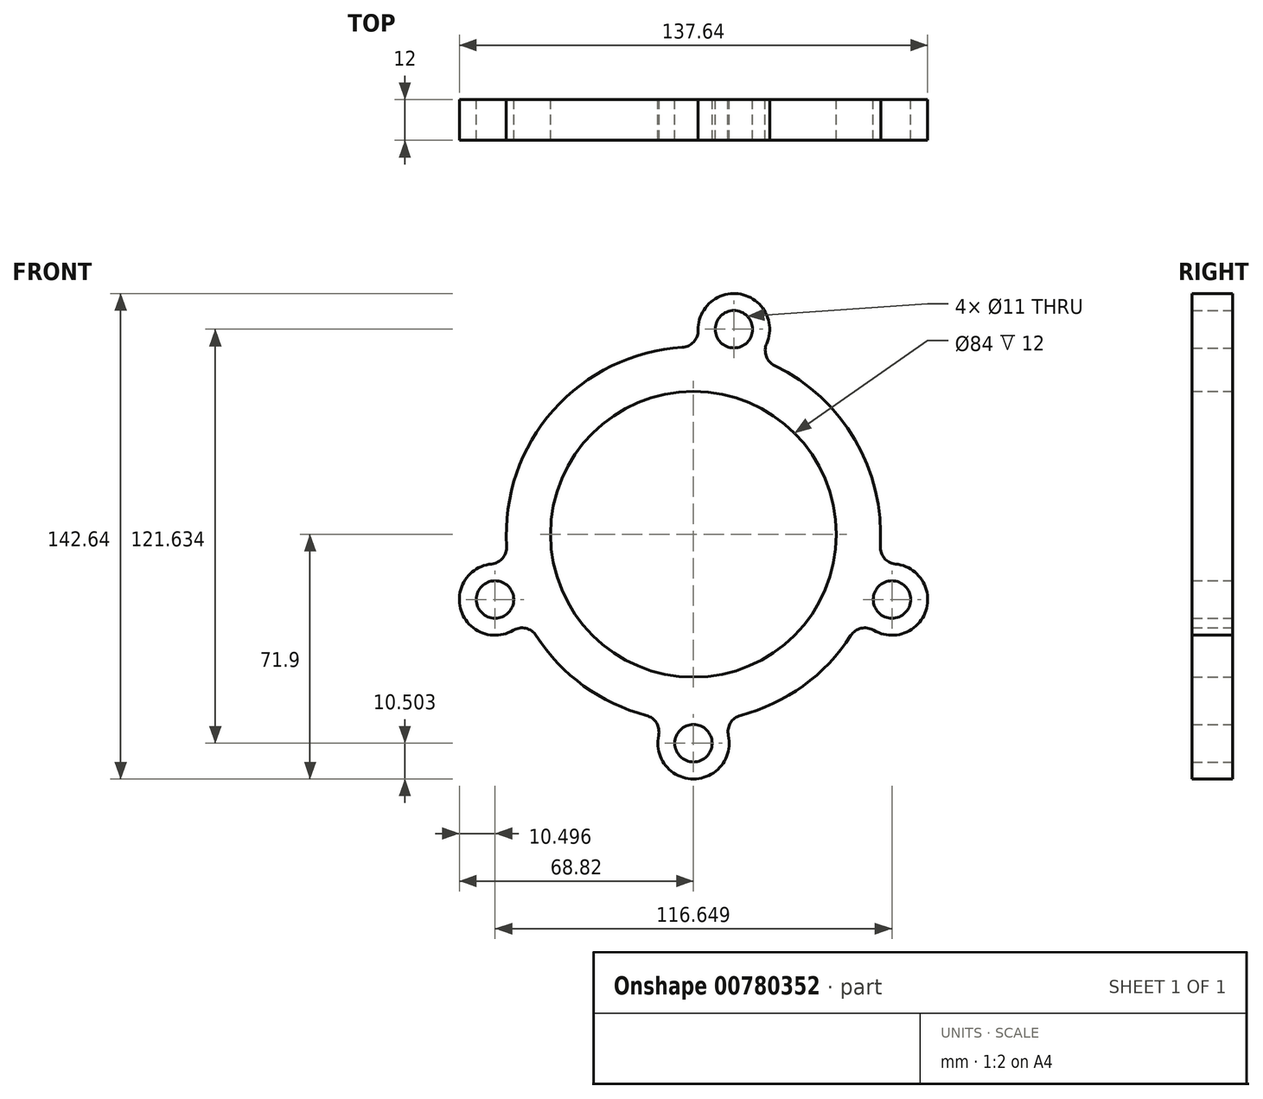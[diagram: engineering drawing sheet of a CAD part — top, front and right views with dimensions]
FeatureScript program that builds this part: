
annotation { "Feature Type Name" : "Feature", "Feature Type Description" : "" }
export const myFeature = defineFeature(function(context is Context, id is Id, definition is map)
    precondition{}
    {
        {
            var Q0;
            Q0=qCreatedBy(makeId("Front.planeOp"),FACE);
            var sketch = newSketch(context, id + "F0", { "sketchPlane" : qUnion([Q0])});
            skCircle(sketch, "E0", {"center": v(0, 0) * mm, "radius": 42 * mm});
            skArc(sketch, "E1.0", {"start": v(-46.22, -29.8) * mm, "mid": v(-32.25, -44.55) * mm, "end": v(-13.87, -53.22) * mm});
            skLineSegment(sketch, "E2", {"start": v(0, 0) * mm, "end": v(-58.32, -19.18) * mm, "construction": true});
            skCircle(sketch, "E3", {"center": v(-58.32, -19.18) * mm, "radius": 5.5 * mm});
            skArc(sketch, "E4.0", {"start": v(-59.38, -8.73) * mm, "mid": v(-68.3, -22.46) * mm, "end": v(-52.97, -28.21) * mm});
            skPoint(sketch, "E5.visualSharp", {"position": v(-49.26, -24.47) * mm});
            skArc(sketch, "E5.filletArc", {"start": v(-46.22, -29.8) * mm, "mid": v(-49.28, -27.65) * mm, "end": v(-52.97, -28.21) * mm});
            skPoint(sketch, "E6.visualSharp", {"position": v(-54.17, -9.54) * mm});
            skArc(sketch, "E6.filletArc", {"start": v(-59.38, -8.73) * mm, "mid": v(-56.07, -7) * mm, "end": v(-54.9, -3.45) * mm});
            skLineSegment(sketch, "E7", {"start": v(0, 0) * mm, "end": v(11.88, 60.24) * mm, "construction": true});
            skLineSegment(sketch, "E8", {"start": v(0, 0) * mm, "end": v(58.32, -19.18) * mm, "construction": true});
            skCircle(sketch, "E9", {"center": v(58.32, -19.18) * mm, "radius": 5.5 * mm});
            skCircle(sketch, "E10", {"center": v(11.88, 60.24) * mm, "radius": 5.5 * mm});
            skLineSegment(sketch, "E11", {"start": v(0, 0) * mm, "end": v(0, -61.4) * mm, "construction": true});
            skCircle(sketch, "E12", {"center": v(0, -61.4) * mm, "radius": 5.5 * mm});
            skArc(sketch, "E13.0", {"start": v(-10.25, -59.14) * mm, "mid": v(0, -71.9) * mm, "end": v(10.25, -59.14) * mm});
            skArc(sketch, "E14.0", {"start": v(52.97, -28.21) * mm, "mid": v(68.3, -22.46) * mm, "end": v(59.38, -8.73) * mm});
            skArc(sketch, "E15.0", {"start": v(21.5, 56.03) * mm, "mid": v(13.91, 70.54) * mm, "end": v(1.38, 60) * mm});
            skArc(sketch, "E16.trimOffspring", {"start": v(13.87, -53.22) * mm, "mid": v(32.25, -44.55) * mm, "end": v(46.22, -29.8) * mm});
            skArc(sketch, "E17.trimOffspring", {"start": v(54.9, -3.45) * mm, "mid": v(47.48, 27.76) * mm, "end": v(23.91, 49.53) * mm});
            skArc(sketch, "E18.trimOffspring", {"start": v(-3.31, 54.9) * mm, "mid": v(-41.2, 36.43) * mm, "end": v(-54.9, -3.45) * mm});
            skPoint(sketch, "E19.visualSharp", {"position": v(-7.86, -54.44) * mm});
            skArc(sketch, "E19.filletArc", {"start": v(-10.25, -59.14) * mm, "mid": v(-10.87, -55.45) * mm, "end": v(-13.87, -53.22) * mm});
            skPoint(sketch, "E20.visualSharp", {"position": v(7.86, -54.44) * mm});
            skArc(sketch, "E20.filletArc", {"start": v(13.87, -53.22) * mm, "mid": v(10.87, -55.45) * mm, "end": v(10.25, -59.14) * mm});
            skPoint(sketch, "E21.visualSharp", {"position": v(49.26, -24.47) * mm});
            skArc(sketch, "E21.filletArc", {"start": v(52.97, -28.21) * mm, "mid": v(49.28, -27.65) * mm, "end": v(46.22, -29.8) * mm});
            skPoint(sketch, "E22.visualSharp", {"position": v(54.17, -9.54) * mm});
            skArc(sketch, "E22.filletArc", {"start": v(54.9, -3.45) * mm, "mid": v(56.07, -7) * mm, "end": v(59.38, -8.73) * mm});
            skPoint(sketch, "E23.visualSharp", {"position": v(18.25, 51.89) * mm});
            skArc(sketch, "E23.filletArc", {"start": v(21.5, 56.03) * mm, "mid": v(21.4, 52.3) * mm, "end": v(23.91, 49.53) * mm});
            skPoint(sketch, "E24.visualSharp", {"position": v(2.82, 54.93) * mm});
            skArc(sketch, "E24.filletArc", {"start": v(-3.31, 54.9) * mm, "mid": v(0.06, 56.5) * mm, "end": v(1.38, 60) * mm});
            skSolve(sketch);
        }
        {
            var Q0;
            Q0=makeQuery(id+"F0.imprint","IMPRINT",FACE,{"disambiguationData":[TD([[makeQuery(id+"F0.imprint","IMPRINT",EDGE,{"derivedFrom":sQuery(id+"F0.wireOp",EDGE,"E0")}),-1.0]])]});
            extrude(context, id + "F1", {"entities" : qUnion([Q0]), "depth" : 12 * mm, "offsetDistance" : 25 * mm});
        }
    });
